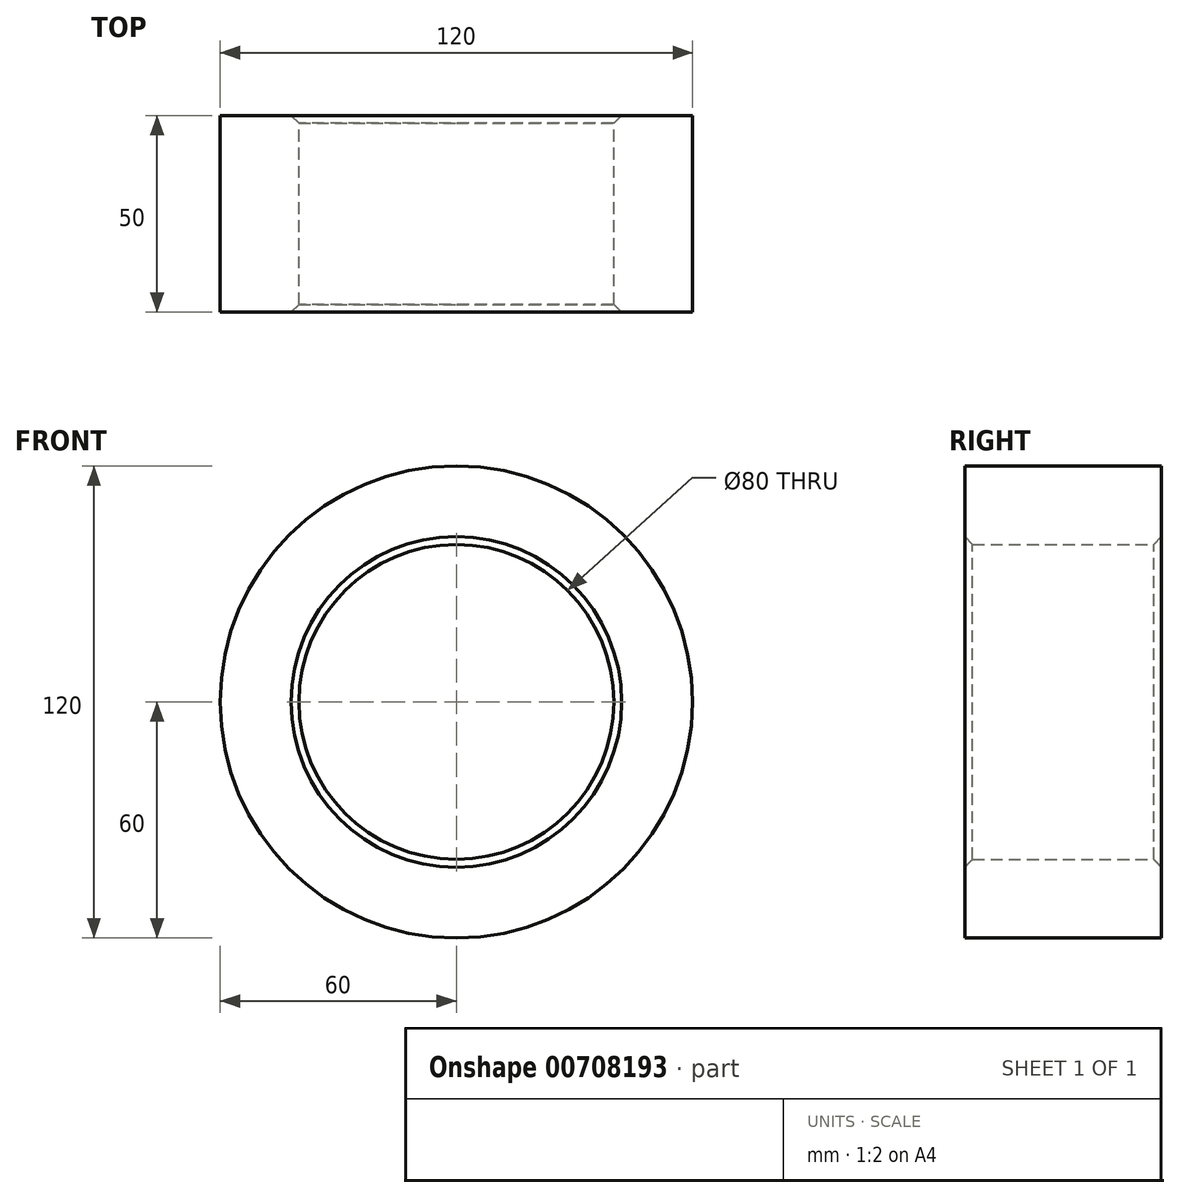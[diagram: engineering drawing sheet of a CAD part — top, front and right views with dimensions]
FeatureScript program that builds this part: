
annotation { "Feature Type Name" : "Feature", "Feature Type Description" : "" }
export const myFeature = defineFeature(function(context is Context, id is Id, definition is map)
    precondition{}
    {
        {
            var Q0;
            Q0=qCreatedBy(makeId("Front.planeOp"),FACE);
            var sketch = newSketch(context, id + "F0", { "sketchPlane" : qUnion([Q0])});
            skCircle(sketch, "E0", {"center": v(0, 0) * mm, "radius": 40 * mm});
            skCircle(sketch, "E1", {"center": v(0, 0) * mm, "radius": 60 * mm});
            skSolve(sketch);
        }
        {
            var Q0;
            Q0=makeQuery(id+"F0.imprint","IMPRINT",FACE,{"disambiguationData":[TD([[makeQuery(id+"F0.imprint","IMPRINT",EDGE,{"derivedFrom":sQuery(id+"F0.wireOp",EDGE,"E0")}),-1.0]])]});
            extrude(context, id + "F1", {"entities" : qUnion([Q0]), "endBound" : BoundingType.SYMMETRIC, "depth" : 50 * mm, "offsetDistance" : 25 * mm});
        }
        {
            var Q0;
            Q0=makeQuery(id+"F1.opExtrude","SWEPT_FACE",FACE,{"disambiguationData":[OSD([sQuery(id+"F0.wireOp",EDGE,"E0")])]});
            chamfer(context, id + "F2", {"entities" : qUnion([Q0]), "width" : 2 * mm, "tangentPropagation" : true});
        }
    });
